# Revit family: BAS-IP_Коммутатор_SH-20-16
name_source: partatom
category: Устройства связи
units: mm (PartAtom-declared; Revit-internal decimal feet)

## family parameters
Всегда вертикально = Да
На основе рабочей плоскости = Нет
Общий = Нет
При загрузке вырезать с полостями = Нет
Размер круглого соединителя = Использовать диаметр
Сохранять ориентацию аннотаций = Нет
Тип детали = Нормальный
Точка расчета площади = Нет

## types (1)
- SH-20.16
    ADSK_Единица измерения = шт.
    ADSK_Завод-изготовитель = BAS-IP
    ADSK_Количество = 1
    ADSK_Марка = SH-20.16
    ADSK_Материал = Gray
    ADSK_Наименование = PoE коммутатор на 16 портов
    Габаритные размеры = 270 × 181 × 44.5 мм
    Изготовитель = BAS-IP
    Источник питания = Переменное напряжение 220 В ±20%, 50 Гц
    Количество портов PoE = 16 x 10/100Base-TX, 8P8C Auto-MDI / MDI-X (IEEE 802.3af)
    Количество портов UpLink = 2 x 10/100Base-TX / 1000Base-T, 8P8C Auto-MDI / MDI-X
    Максимальная длина кабеля при подключении к портам с PoE = 100 м
    Максимальная мощность на каждом порту с PoE = 15,4 Вт
    Максимальная суммарная мощность всех портов = 246 Вт
    Метод подачи питания на портах с PoE = Метод B
    Температурный режим = -20 – +55 °С
    Уровень коммутатора = 1 (неуправляемый)
